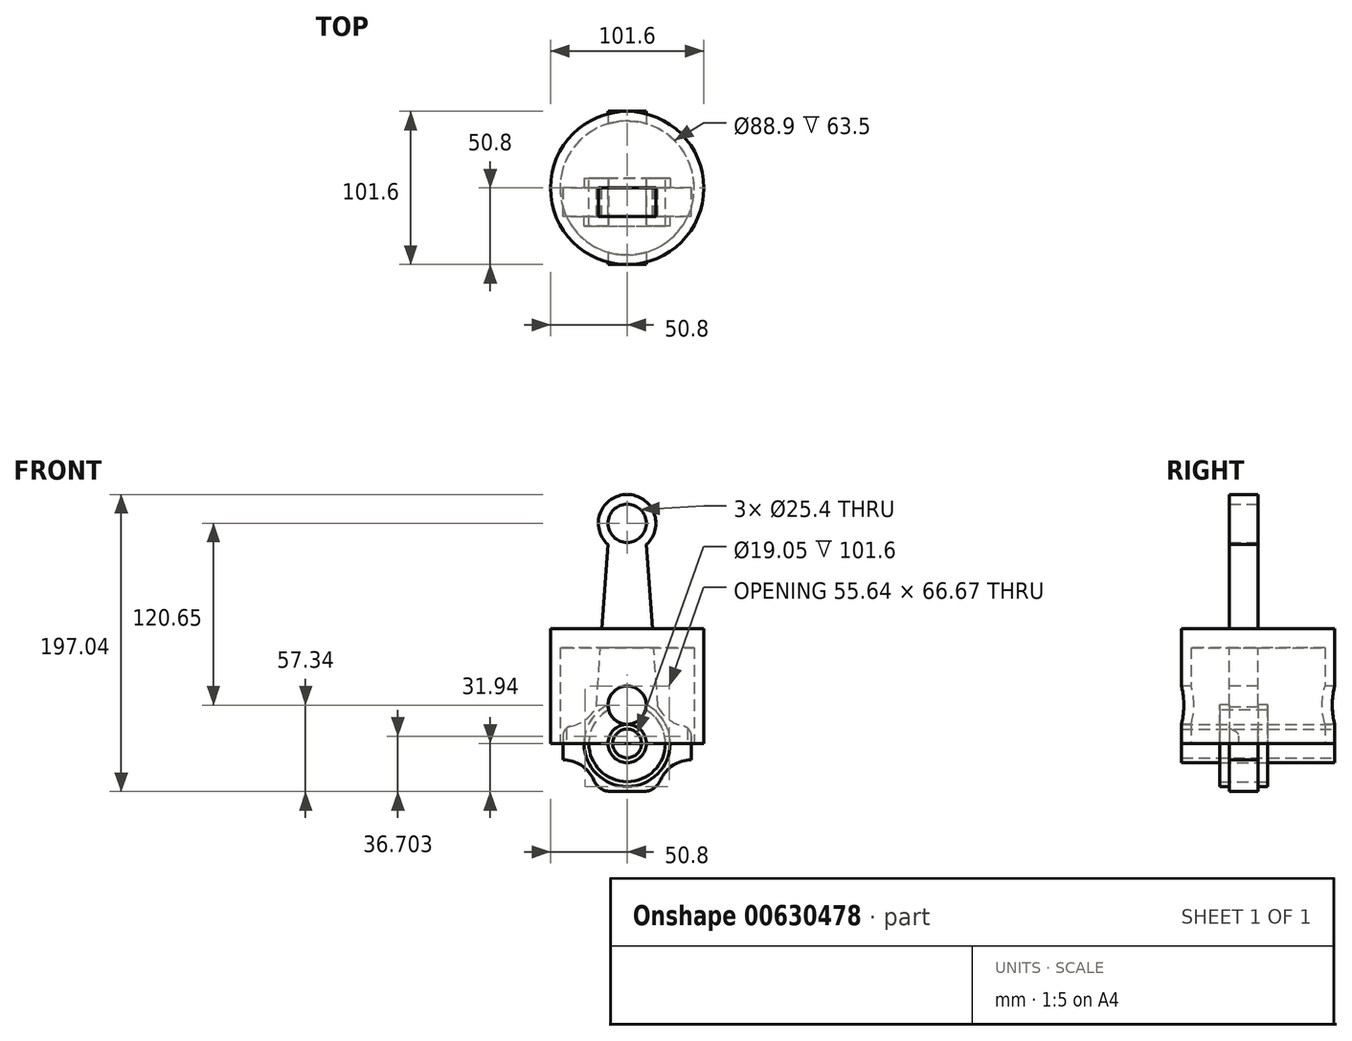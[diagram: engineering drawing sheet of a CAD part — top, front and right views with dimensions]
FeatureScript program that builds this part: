
annotation { "Feature Type Name" : "Feature", "Feature Type Description" : "" }
export const myFeature = defineFeature(function(context is Context, id is Id, definition is map)
    precondition{}
    {
        {
            var Q0;
            Q0=qCreatedBy(makeId("Front.planeOp"),FACE);
            var sketch = newSketch(context, id + "F0", { "sketchPlane" : qUnion([Q0])});
            skCircle(sketch, "E0", {"center": v(0, 0) * mm, "radius": 28.58 * mm});
            skLineSegment(sketch, "E1", {"start": v(0, 31.75) * mm, "end": v(0, 133.35) * mm});
            skLineSegment(sketch, "E2", {"start": v(-20.4, 24.32) * mm, "end": v(-12.7, 133.35) * mm});
            skLineSegment(sketch, "E3", {"start": v(20.4, 24.32) * mm, "end": v(12.7, 133.35) * mm});
            skLineSegment(sketch, "E4", {"start": v(-42.54, 10.86) * mm, "end": v(-42.54, -10.86) * mm});
            skLineSegment(sketch, "E5", {"start": v(42.54, -10.86) * mm, "end": v(42.54, 10.86) * mm});
            skArc(sketch, "E6", {"start": v(-42.54, 10.86) * mm, "mid": v(-29.58, 14.49) * mm, "end": v(-20.4, 24.32) * mm});
            skArc(sketch, "E7", {"start": v(20.4, 24.32) * mm, "mid": v(29.58, 14.49) * mm, "end": v(42.54, 10.86) * mm});
            skPoint(sketch, "E8.start.orphan", {"position": v(-31.75, 0) * mm});
            skLineSegment(sketch, "E9", {"start": v(0, -28.58) * mm, "end": v(0, -31.75) * mm});
            skLineSegment(sketch, "E10", {"start": v(20.4, -31.94) * mm, "end": v(-20.4, -31.94) * mm});
            skArc(sketch, "E11", {"start": v(42.54, -10.86) * mm, "mid": v(27.25, -16.97) * mm, "end": v(20.4, -31.94) * mm});
            skArc(sketch, "E12", {"start": v(-20.4, -31.94) * mm, "mid": v(-27.25, -16.97) * mm, "end": v(-42.54, -10.86) * mm});
            skLineSegment(sketch, "E13", {"start": v(0, 133.35) * mm, "end": v(0, 146.05) * mm});
            skArc(sketch, "E14", {"start": v(12.8, 131.94) * mm, "mid": v(0, 165.1) * mm, "end": v(-12.8, 131.94) * mm});
            skCircle(sketch, "E15", {"center": v(0, 146.05) * mm, "radius": 12.7 * mm});
            skSolve(sketch);
        }
        {
            var Q0;
            Q0 = qSketchRegion(id + "F0", true);
            extrude(context, id + "F1", {"entities" : qUnion([Q0]), "depth" : 19.05 * mm, "offsetDistance" : 25.4 * mm});
        }
        {
            var Q0;
            Q0=qCreatedBy(makeId("Front.planeOp"),FACE);
            var sketch = newSketch(context, id + "F2", { "sketchPlane" : qUnion([Q0])});
            skCircle(sketch, "E16", {"center": v(0, 0) * mm, "radius": 28.57 * mm});
            skCircle(sketch, "E17", {"center": v(0, 0) * mm, "radius": 25.4 * mm});
            skSolve(sketch);
        }
        {
            var Q0;
            Q0 = qSketchRegion(id + "F2", true);
            extrude(context, id + "F3", {"entities" : qUnion([Q0]), "operationType" : NewBodyOperationType.ADD, "depth" : 25.4 * mm, "offsetDistance" : 25.4 * mm});
        }
        {
            var Q0;
            Q0=makeQuery(id+"F3.boolean.opBoolean","MERGE",FACE,{"derivedFrom":[makeQuery(id+"F1.opExtrude","CAP_FACE",FACE,{"disambiguationData":[OSD([sQuery(id+"F0.wireOp",EDGE,"E0"),sQuery(id+"F0.wireOp",EDGE,"E2"),sQuery(id+"F0.wireOp",EDGE,"E3"),sQuery(id+"F0.wireOp",EDGE,"E4"),sQuery(id+"F0.wireOp",EDGE,"E5"),sQuery(id+"F0.wireOp",EDGE,"E6"),sQuery(id+"F0.wireOp",EDGE,"E7"),sQuery(id+"F0.wireOp",EDGE,"E10"),sQuery(id+"F0.wireOp",EDGE,"E11"),sQuery(id+"F0.wireOp",EDGE,"E12"),sQuery(id+"F0.wireOp",EDGE,"E14"),sQuery(id+"F0.wireOp",EDGE,"E15")])],"isStart":true}),makeQuery(id+"F3.opExtrude","CAP_FACE",FACE,{"disambiguationData":[OSD([sQuery(id+"F2.wireOp",EDGE,"E16"),sQuery(id+"F2.wireOp",EDGE,"E17")])],"isStart":true})]});
            var sketch = newSketch(context, id + "F4", { "sketchPlane" : qUnion([Q0])});
            skCircle(sketch, "E18", {"center": v(0, 0) * mm, "radius": 28.58 * mm});
            skCircle(sketch, "E19", {"center": v(0, 0) * mm, "radius": 25.4 * mm});
            skSolve(sketch);
        }
        {
            var Q0;
            Q0 = qSketchRegion(id + "F4", true);
            extrude(context, id + "F5", {"entities" : qUnion([Q0]), "operationType" : NewBodyOperationType.ADD, "depth" : 6.35 * mm, "offsetDistance" : 25.4 * mm});
        }
        {
            var Q0;
            Q0=makeQuery(id+"F1.opExtrude","SWEPT_EDGE",EDGE,{"disambiguationData":[OSD([sQuery(id+"F0.wireOp",EDGE,"E10"),sQuery(id+"F0.wireOp",EDGE,"E11")])]});
            var Q1;
            Q1=makeQuery(id+"F1.opExtrude","SWEPT_EDGE",EDGE,{"disambiguationData":[OSD([sQuery(id+"F0.wireOp",EDGE,"E10"),sQuery(id+"F0.wireOp",EDGE,"E12")])]});
            fillet(context, id + "F6", {"entities" : qUnion([Q0, Q1]), "radius" : 12.7 * mm, "tangentPropagation" : true, "allowEdgeOverflow" : false});
        }
        {
            var Q0;
            Q0=makeQuery(id+"F1.opExtrude","SWEPT_EDGE",EDGE,{"disambiguationData":[OSD([sQuery(id+"F0.wireOp",EDGE,"E5"),sQuery(id+"F0.wireOp",EDGE,"E7")])]});
            var Q1;
            Q1=makeQuery(id+"F1.opExtrude","SWEPT_EDGE",EDGE,{"disambiguationData":[OSD([sQuery(id+"F0.wireOp",EDGE,"E4"),sQuery(id+"F0.wireOp",EDGE,"E6")])]});
            fillet(context, id + "F7", {"entities" : qUnion([Q0, Q1]), "radius" : 6.35 * mm, "tangentPropagation" : true, "allowEdgeOverflow" : false});
        }
        {
            var Q0;
            Q0=qCreatedBy(makeId("Front.planeOp"),FACE);
            var sketch = newSketch(context, id + "F8", { "sketchPlane" : qUnion([Q0])});
            skCircle(sketch, "E20", {"center": v(0, 0) * mm, "radius": 12.7 * mm});
            skCircle(sketch, "E21", {"center": v(0, 0) * mm, "radius": 9.53 * mm});
            skSolve(sketch);
        }
        {
            var Q0;
            Q0 = qSketchRegion(id + "F8", true);
            extrude(context, id + "F9", {"entities" : qUnion([Q0]), "depth" : 50.8 * mm, "offsetDistance" : 25.4 * mm, "hasSecondDirection" : true, "secondDirectionOppositeDirection" : true, "secondDirectionDepth" : 50.8 * mm});
        }
        {
            var Q0;
            Q0=qCreatedBy(makeId("Top.planeOp"),FACE);
            var sketch = newSketch(context, id + "F10", { "sketchPlane" : qUnion([Q0])});
            skCircle(sketch, "E22", {"center": v(0, 0) * mm, "radius": 50.8 * mm});
            skCircle(sketch, "E23", {"center": v(0, 0) * mm, "radius": 44.45 * mm});
            skSolve(sketch);
        }
        {
            var Q0;
            Q0 = qSketchRegion(id + "F10", true);
            extrude(context, id + "F11", {"entities" : qUnion([Q0]), "depth" : 76.2 * mm, "offsetDistance" : 25.4 * mm});
        }
        {
            var Q0;
            Q0=makeQuery(id+"F11.opExtrude","CAP_FACE",FACE,{"disambiguationData":[OSD([sQuery(id+"F10.wireOp",EDGE,"E22"),sQuery(id+"F10.wireOp",EDGE,"E23")])],"isStart":false});
            var sketch = newSketch(context, id + "F12", { "sketchPlane" : qUnion([Q0])});
            skCircle(sketch, "E24", {"center": v(0, 0) * mm, "radius": 50.8 * mm});
            skSolve(sketch);
        }
        {
            var Q0;
            Q0 = qSketchRegion(id + "F12", true);
            extrude(context, id + "F13", {"entities" : qUnion([Q0]), "operationType" : NewBodyOperationType.ADD, "oppositeDirection" : true, "depth" : 12.7 * mm, "offsetDistance" : 25.4 * mm});
        }
        {
            var Q0;
            Q0=qCreatedBy(makeId("Front.planeOp"),FACE);
            var sketch = newSketch(context, id + "F14", { "sketchPlane" : qUnion([Q0])});
            skLineSegment(sketch, "E25", {"start": v(0, 0) * mm, "end": v(0, 25.4) * mm});
            skCircle(sketch, "E26", {"center": v(0, 25.4) * mm, "radius": 12.7 * mm});
            skSolve(sketch);
        }
        {
            var Q0;
            Q0 = qSketchRegion(id + "F14", true);
            extrude(context, id + "F15", {"entities" : qUnion([Q0]), "operationType" : NewBodyOperationType.REMOVE, "oppositeDirection" : true, "depth" : 72.14 * mm, "offsetDistance" : 25.4 * mm, "hasSecondDirection" : true, "secondDirectionOppositeDirection" : false, "secondDirectionDepth" : 101.35 * mm});
        }
    });
